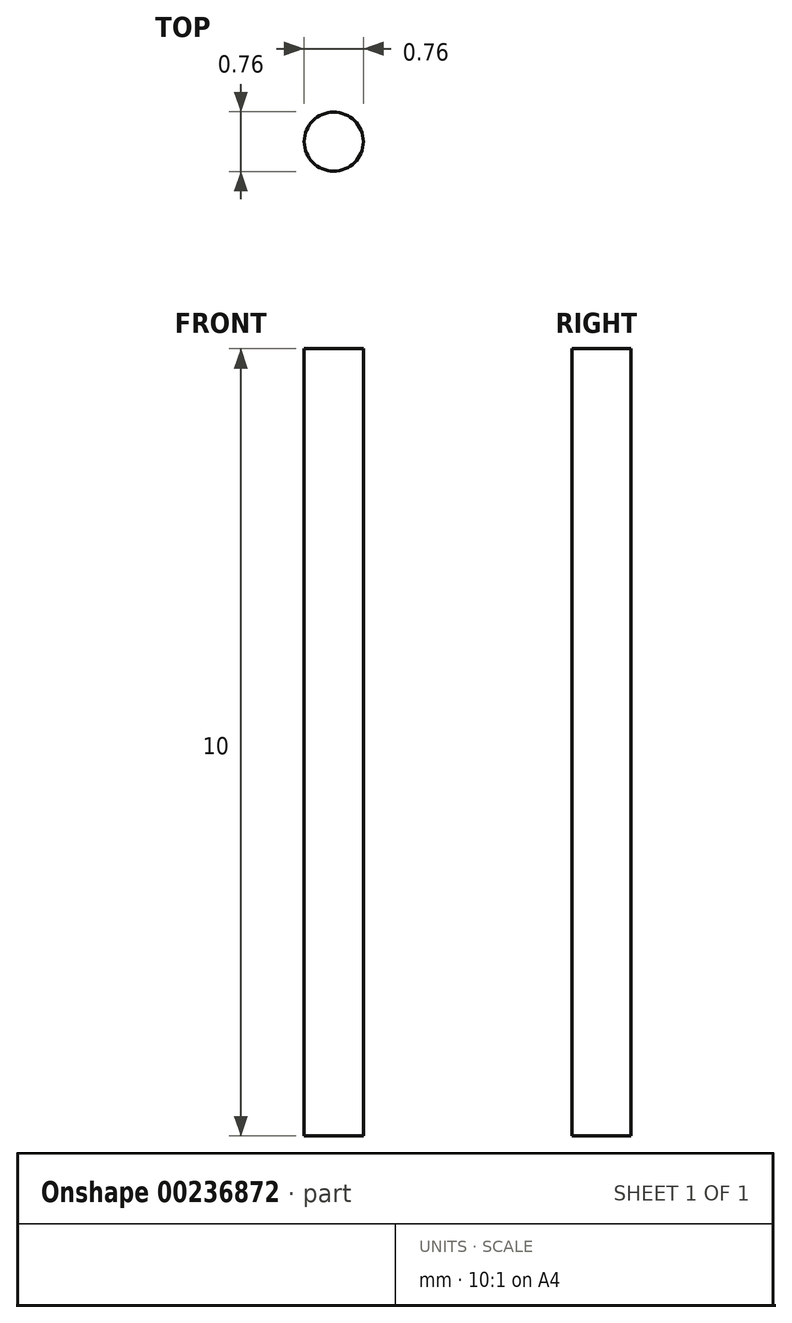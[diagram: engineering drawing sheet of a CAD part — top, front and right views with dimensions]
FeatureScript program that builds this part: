
annotation { "Feature Type Name" : "Feature", "Feature Type Description" : "" }
export const myFeature = defineFeature(function(context is Context, id is Id, definition is map)
    precondition{}
    {
        {
            var Q0;
            Q0=qCreatedBy(makeId("Top.planeOp"),FACE);
            var sketch = newSketch(context, id + "F0", { "sketchPlane" : qUnion([Q0])});
            skCircle(sketch, "E0", {"center": v(0, 0) * mm, "radius": 0.38 * mm});
            skSolve(sketch);
        }
        {
            var Q0;
            Q0 = qSketchRegion(id + "F0", true);
            extrude(context, id + "F1", {"entities" : qUnion([Q0]), "depth" : 10 * mm});
        }
    });
